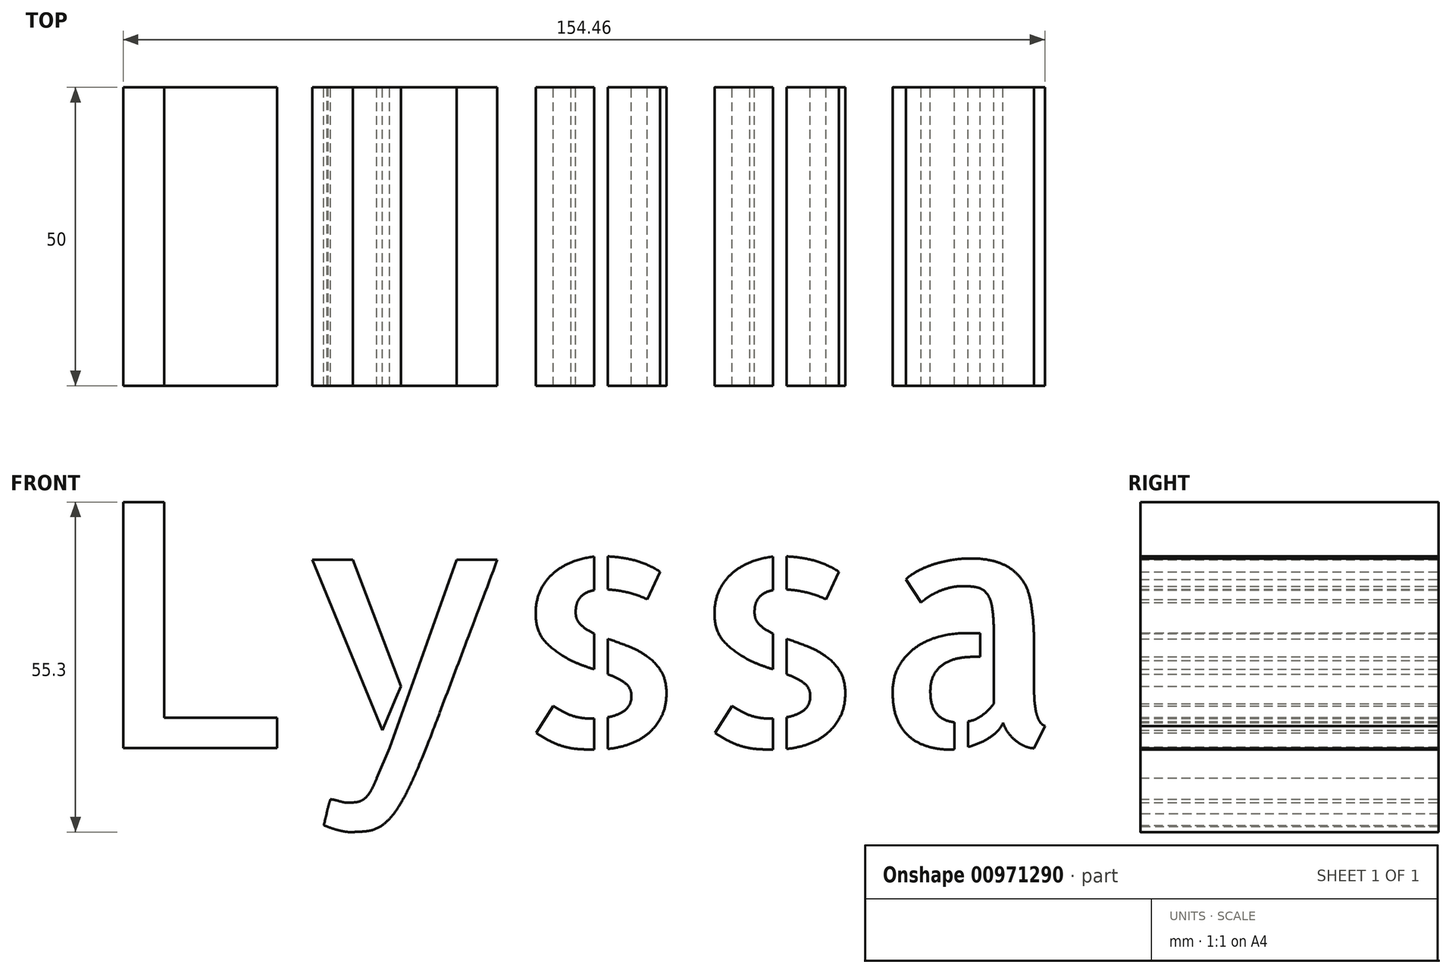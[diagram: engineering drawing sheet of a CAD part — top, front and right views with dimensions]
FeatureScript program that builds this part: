
annotation { "Feature Type Name" : "Feature", "Feature Type Description" : "" }
export const myFeature = defineFeature(function(context is Context, id is Id, definition is map)
    precondition{}
    {
        {
            var Q0;
            Q0=qCreatedBy(makeId("Front.planeOp"),FACE);
            var sketch = newSketch(context, id + "F0", { "sketchPlane" : qUnion([Q0])});
            skText(sketch, "E0", { "text": "Lyssa", "fontName": "AllertaStencil-Regular.ttf"});
            const initialGuessF0  = {"E0": [-0.12077, 0, 1, 0, 0.04123]};
            skSetInitialGuess(sketch, initialGuessF0);
            skSolve(sketch);
        }
        {
            var Q0;
            Q0 = qSketchRegion(id + "F0", true);
            extrude(context, id + "F1", {"entities" : qUnion([Q0]), "depth" : 50 * mm, "offsetDistance" : 25 * mm});
        }
    });
